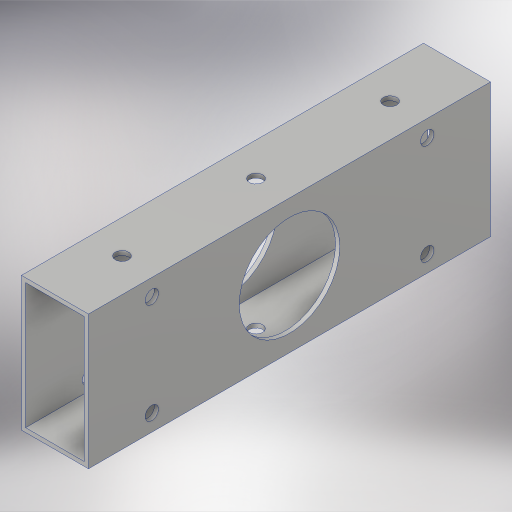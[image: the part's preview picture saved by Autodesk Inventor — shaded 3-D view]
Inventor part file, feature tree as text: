
AUTODESK INVENTOR PART (.ipt)
format: ipt  version: 2023.4 (Build 274418000, 418)  size: 320,000 bytes
history: native  units: in
note: dims shown in document units (in); Inventor stores cm internally (conversion verified against a paired STEP export)
features: sketch x4, hole x3, extrude x2, projected_geometry x1
ambient origin geometry x8: Origin, YZ Plane, XZ Plane, XY Plane, X Axis, Y Axis, Z Axis, Center Point
bodies: Solid1 (feature_tree)
feature tree (10):
  extrude  "Extrusion1"  Depth=4.0in
  hole  "Hole1"  [1 undecoded]
  hole  "Hole3"  [1 undecoded]
  extrude  "Extrusion2"  Depth=1.0in
  hole  "Hole2"  [1 undecoded]
  sketch  "Sketch2"  dims[d4=0.0in d5=4.0in]
  projected_geometry  "Projected Loop1"
  sketch  "Sketch3"  dims[d6=0.201in d7=0.75in d8=0.385in d9=0.25in d10=0.5635in d11=1.0in d12=0.8108in d14=4.7244in]
  sketch  "Sketch4"  dims[d15=3.7402in d16=4.2323in]
  sketch  "Sketch5"  dims[d17=1.5in d18=0.156in d19=0.38in d20=0.375in d21=0.25in d22=0.5635in d23=1.0in d24=0.8108in d28=1.5in d29=0.201in d30=0.38in d31=0.385in d32=0.25in d33=0.5635in d34=1.0in d35=0.8108in d36=1.5in d37=1.0in d38=0.0in d39=4.1098in]
note: 3 required parameter values undecoded (feature->parameter linkage not recoverable at this tier; creation-order binding heuristic only, values carry confidence <= 0.55)
